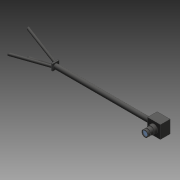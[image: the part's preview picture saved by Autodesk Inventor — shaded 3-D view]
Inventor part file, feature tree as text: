
AUTODESK INVENTOR PART (.ipt)
format: ipt  version: 2016 (Build 200138000, 138)  size: 176,640 bytes
history: native  units: mm
features: sketch x10, extrude x8, loft x3, plane x2, projected_geometry x1
ambient origin geometry x8: Origin, YZ Plane, XZ Plane, XY Plane, X Axis, Y Axis, Z Axis, Center Point
bodies: 实体1 (feature_tree)
feature tree (24):
  extrude  "拉伸1"  Depth=2.0mm TaperAngle=0.0deg
  extrude  "拉伸2"  Depth=1.0mm TaperAngle=0.0deg
  extrude  "拉伸3"  Depth=1.0mm TaperAngle=0.0deg
  extrude  "拉伸4"  Depth=5.0mm TaperAngle=0.0deg
  extrude  "拉伸5"  Depth=15.0mm TaperAngle=0.0deg
  extrude  "拉伸6"  Depth=150.0mm TaperAngle=0.0deg
  extrude  "拉伸7"  Depth=2.0mm TaperAngle=0.0deg
  extrude  "拉伸8"  TaperAngle=120.0deg  [1 undecoded]
  sketch  "草图9"  dims[d24=3.0mm d26=3.0mm]
  plane  "工作平面2"
  sketch  "草图10"  dims[d27=3.0mm d31=51.499mm d32=4.0mm d33=4.0mm d34=30.0mm d35=20.0mm d36=0.0mm d37=90.0deg d38=0.0mm d39=90.0deg d40=0.0mm d41=90.0deg d42=0.0mm d43=90.0deg d44=0.0mm d45=90.0deg d46=0.0mm d47=90.0deg]
  loft  "放样1"
  loft  "放样2"
  loft  "放样3"
  sketch  "草图1"  dims[d0=10.0mm d1=2.0mm d2=0.0mm]
  sketch  "草图2"  dims[d3=8.0mm d4=1.0mm d5=0.0mm]
  projected_geometry  "投影回路1"
  sketch  "草图3"  dims[d6=5.0mm d7=0.0mm d8=1.0mm d9=0.0mm]
  sketch  "草图4"  dims[d10=12.0mm d11=5.0mm d12=0.0mm]
  sketch  "草图5"  dims[d13=20.0mm d14=15.0mm d15=0.0mm]
  sketch  "草图6"  dims[d16=7.0mm d17=150.0mm d18=0.0mm]
  sketch  "草图7"  dims[d19=10.0mm d20=2.0mm d21=0.0mm]
  sketch  "草图8"  dims[d22=120.0deg d23=120.0deg]
  plane  "工作平面1"
note: 1 required parameter value undecoded (feature->parameter linkage not recoverable at this tier; creation-order binding heuristic only, values carry confidence <= 0.55)
